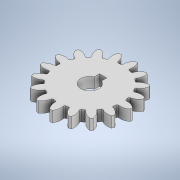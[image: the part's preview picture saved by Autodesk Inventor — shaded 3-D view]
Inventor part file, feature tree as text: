
AUTODESK INVENTOR PART (.ipt)
format: ipt  version: 2020 (Build 240168000, 168)  size: 262,144 bytes
history: native  units: mm
features: extrude x2, sketch x2, pattern_circular x1
ambient origin geometry x8: Origin, YZ Plane, XZ Plane, XY Plane, X Axis, Y Axis, Z Axis, Center Point
bodies: Solid1 (feature_tree)
feature tree (5):
  extrude  "Extrusion1"  Depth=3.0mm
  pattern_circular  "Circular Pattern2"  [2 undecoded]
  extrude  "Extrusion2"  TaperAngle=0.0deg  [1 undecoded]
  sketch  "Sketch1"  dims[d4=3.0mm d5=0.0mm d13=5.0mm]
  sketch  "Sketch2"  dims[d14=2.0mm d15=3.7mm d16=0.0mm d17=0.0mm d18=170.0mm d19=360.0deg d23=21.0mm d25=1.544118mm d26=1.235294mm d27=3.490659mm d28=19.733545mm d29=3.490659mm d30=0.308824mm d31=0.617647mm d32=0.9702mm]
note: 3 required parameter values undecoded (feature->parameter linkage not recoverable at this tier; creation-order binding heuristic only, values carry confidence <= 0.55)
